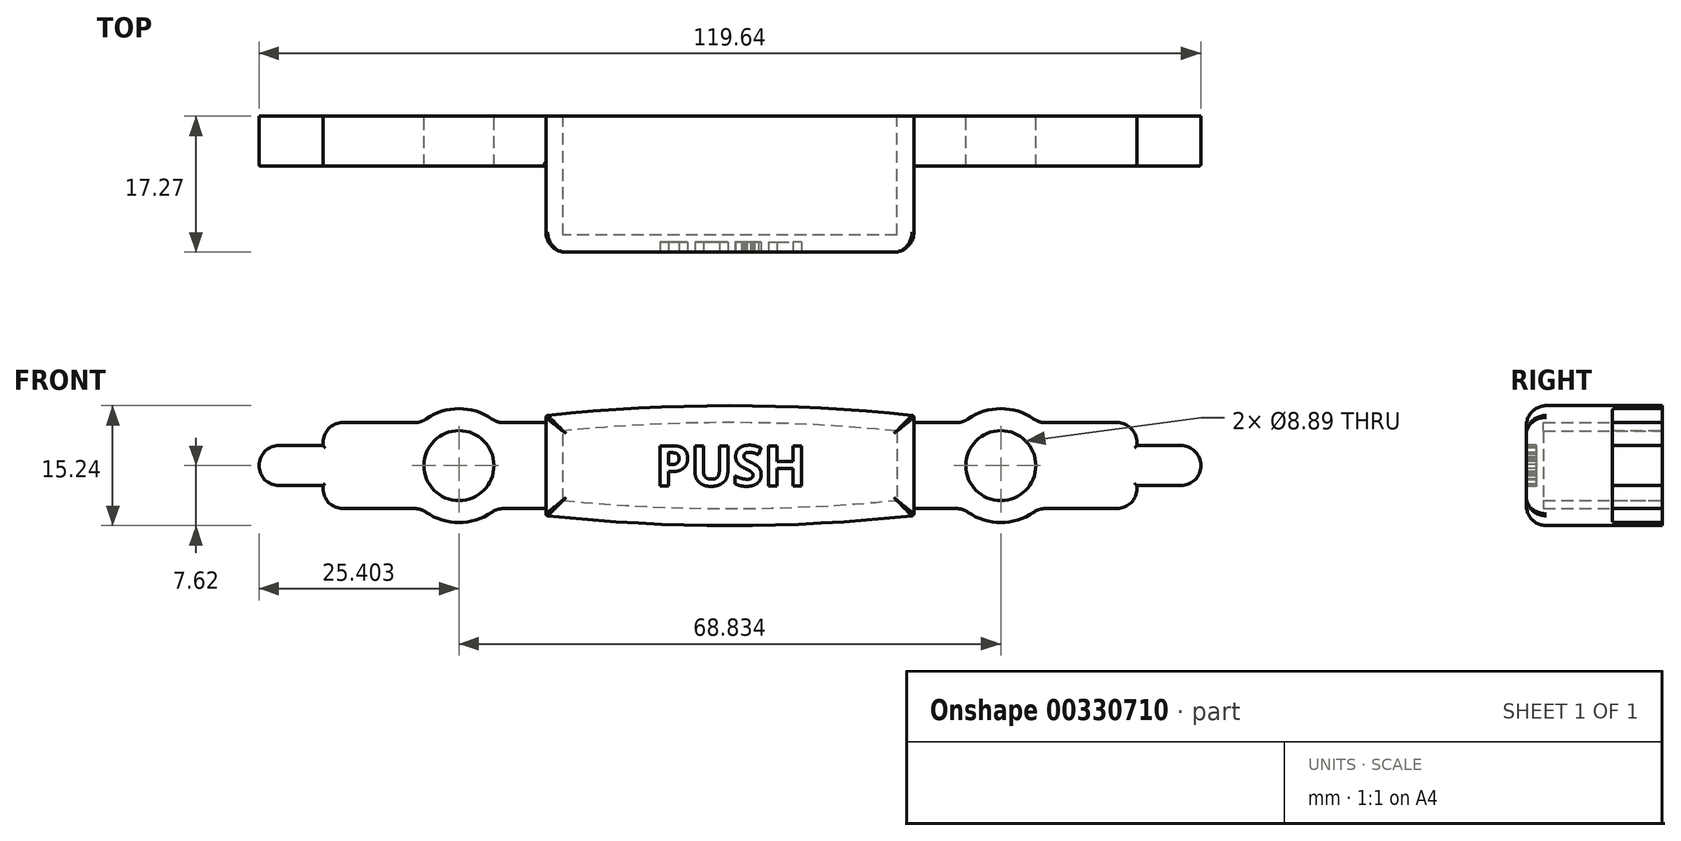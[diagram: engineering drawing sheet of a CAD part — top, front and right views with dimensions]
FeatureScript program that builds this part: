
annotation { "Feature Type Name" : "Feature", "Feature Type Description" : "" }
export const myFeature = defineFeature(function(context is Context, id is Id, definition is map)
    precondition{}
    {
        {
            var Q0;
            Q0=qCreatedBy(makeId("Front.planeOp"),FACE);
            var sketch = newSketch(context, id + "F0", { "sketchPlane" : qUnion([Q0])});
            skLineSegment(sketch, "E0", {"start": v(23.37, 6.35) * mm, "end": v(23.37, -6.35) * mm});
            skLineSegment(sketch, "E1", {"start": v(-23.37, -6.35) * mm, "end": v(-23.37, 6.35) * mm});
            skArc(sketch, "E2", {"start": v(23.37, 6.35) * mm, "mid": v(0, 7.62) * mm, "end": v(-23.37, 6.35) * mm});
            skArc(sketch, "E3", {"start": v(-23.37, -6.35) * mm, "mid": v(0, -7.62) * mm, "end": v(23.37, -6.35) * mm});
            skSolve(sketch);
        }
        {
            var Q0;
            Q0=qCreatedBy(makeId("Front.planeOp"),FACE);
            var sketch = newSketch(context, id + "F1", { "sketchPlane" : qUnion([Q0])});
            skLineSegment(sketch, "E4", {"start": v(23.26, 5.46) * mm, "end": v(29.67, 5.46) * mm});
            skLineSegment(sketch, "E5", {"start": v(51.69, 5.46) * mm, "end": v(51.69, 2.54) * mm});
            skLineSegment(sketch, "E6", {"start": v(51.69, -5.46) * mm, "end": v(39.17, -5.46) * mm});
            skLineSegment(sketch, "E7", {"start": v(51.69, -2.54) * mm, "end": v(59.82, -2.54) * mm});
            skLineSegment(sketch, "E8", {"start": v(59.82, 2.54) * mm, "end": v(59.82, -2.54) * mm});
            skLineSegment(sketch, "E9", {"start": v(59.82, 2.54) * mm, "end": v(51.69, 2.54) * mm});
            skCircle(sketch, "E10", {"center": v(34.42, 0) * mm, "radius": 4.44 * mm});
            skArc(sketch, "E11", {"start": v(29.67, -5.46) * mm, "mid": v(34.42, -7.24) * mm, "end": v(39.17, -5.46) * mm});
            skLineSegment(sketch, "E12.trimOffspring", {"start": v(51.69, -2.54) * mm, "end": v(51.69, -5.46) * mm});
            skLineSegment(sketch, "E13.trimOffspring", {"start": v(39.17, 5.46) * mm, "end": v(51.69, 5.46) * mm});
            skLineSegment(sketch, "E14.trimOffspring", {"start": v(29.67, -5.46) * mm, "end": v(23.26, -5.46) * mm});
            skLineSegment(sketch, "E15", {"start": v(23.26, 5.46) * mm, "end": v(23.26, -5.46) * mm});
            skArc(sketch, "E16.trimOffspring", {"start": v(39.17, 5.46) * mm, "mid": v(34.42, 7.24) * mm, "end": v(29.67, 5.46) * mm});
            skPoint(sketch, "E17.orphan", {"position": v(21.72, 5.46) * mm});
            skPoint(sketch, "E18.orphan", {"position": v(21.72, -5.46) * mm});
            skLineSegment(sketch, "E19.MirrorCS", {"start": v(-51.69, -2.54) * mm, "end": v(-51.69, -5.46) * mm});
            skLineSegment(sketch, "E20.MirrorCS", {"start": v(-51.69, 5.46) * mm, "end": v(-51.69, 2.54) * mm});
            skPoint(sketch, "E21.MirrorP", {"position": v(-21.72, 5.46) * mm});
            skLineSegment(sketch, "E22.MirrorCS", {"start": v(-23.26, 5.46) * mm, "end": v(-29.67, 5.46) * mm});
            skPoint(sketch, "E23.MirrorP", {"position": v(-21.72, -5.46) * mm});
            skArc(sketch, "E24.MirrorCS", {"start": v(-39.17, 5.46) * mm, "mid": v(-34.42, 7.24) * mm, "end": v(-29.67, 5.46) * mm});
            skLineSegment(sketch, "E25.MirrorCS", {"start": v(-59.82, 2.54) * mm, "end": v(-51.69, 2.54) * mm});
            skArc(sketch, "E26.MirrorCS", {"start": v(-29.67, -5.46) * mm, "mid": v(-34.42, -7.24) * mm, "end": v(-39.17, -5.46) * mm});
            skLineSegment(sketch, "E27.MirrorCS", {"start": v(-51.69, -5.46) * mm, "end": v(-39.17, -5.46) * mm});
            skCircle(sketch, "E28.MirrorC", {"center": v(-34.42, 0) * mm, "radius": 4.44 * mm});
            skLineSegment(sketch, "E29.MirrorCS", {"start": v(-39.17, 5.46) * mm, "end": v(-51.69, 5.46) * mm});
            skLineSegment(sketch, "E30.MirrorCS", {"start": v(-59.82, 2.54) * mm, "end": v(-59.82, -2.54) * mm});
            skLineSegment(sketch, "E31.MirrorCS", {"start": v(-51.69, -2.54) * mm, "end": v(-59.82, -2.54) * mm});
            skLineSegment(sketch, "E32.MirrorCS", {"start": v(-29.67, -5.46) * mm, "end": v(-23.26, -5.46) * mm});
            skLineSegment(sketch, "E33.MirrorCS", {"start": v(-23.26, 5.46) * mm, "end": v(-23.26, -5.46) * mm});
            skSolve(sketch);
        }
        {
            var Q0;
            Q0=makeQuery(id+"F0.imprint","IMPRINT",FACE,{"disambiguationData":[TD([[makeQuery(id+"F0.imprint","IMPRINT",EDGE,{"derivedFrom":sQuery(id+"F0.wireOp",EDGE,"E0")}),-1.0]])]});
            extrude(context, id + "F2", {"entities" : qUnion([Q0]), "depth" : 17.27 * mm});
        }
        {
            var Q0;
            Q0=makeQuery(id+"F2.opExtrude","CAP_FACE",FACE,{"disambiguationData":[OSD([sQuery(id+"F0.wireOp",EDGE,"E0"),sQuery(id+"F0.wireOp",EDGE,"E1"),sQuery(id+"F0.wireOp",EDGE,"E2"),sQuery(id+"F0.wireOp",EDGE,"E3")])],"isStart":true});
            shell(context, id + "F3", {"entities" : qUnion([Q0]), "thickness" : 2.16 * mm});
        }
        {
            var Q0;
            Q0 = qSketchRegion(id + "F1", true);
            extrude(context, id + "F4", {"entities" : qUnion([Q0]), "operationType" : NewBodyOperationType.ADD, "depth" : 6.35 * mm});
        }
        {
            var Q0;
            Q0=makeQuery(id+"F4.opExtrude","SWEPT_EDGE",EDGE,{"disambiguationData":[OSD([sQuery(id+"F1.wireOp",EDGE,"E30.MirrorCS"),sQuery(id+"F1.wireOp",EDGE,"E31.MirrorCS")])]});
            var Q1;
            Q1=makeQuery(id+"F4.opExtrude","SWEPT_EDGE",EDGE,{"disambiguationData":[OSD([sQuery(id+"F1.wireOp",EDGE,"E25.MirrorCS"),sQuery(id+"F1.wireOp",EDGE,"E30.MirrorCS")])]});
            var Q2;
            Q2=makeQuery(id+"F4.opExtrude","SWEPT_EDGE",EDGE,{"disambiguationData":[OSD([sQuery(id+"F1.wireOp",EDGE,"E7"),sQuery(id+"F1.wireOp",EDGE,"E8")])]});
            var Q3;
            Q3=makeQuery(id+"F4.opExtrude","SWEPT_EDGE",EDGE,{"disambiguationData":[OSD([sQuery(id+"F1.wireOp",EDGE,"E8"),sQuery(id+"F1.wireOp",EDGE,"E9")])]});
            var Q4;
            Q4=makeQuery(id+"F4.opExtrude","SWEPT_EDGE",EDGE,{"disambiguationData":[OSD([sQuery(id+"F1.wireOp",EDGE,"E5"),sQuery(id+"F1.wireOp",EDGE,"E13.trimOffspring")])]});
            var Q5;
            Q5=makeQuery(id+"F4.opExtrude","SWEPT_EDGE",EDGE,{"disambiguationData":[OSD([sQuery(id+"F1.wireOp",EDGE,"E6"),sQuery(id+"F1.wireOp",EDGE,"E12.trimOffspring")])]});
            var Q6;
            Q6=makeQuery(id+"F4.opExtrude","SWEPT_EDGE",EDGE,{"disambiguationData":[OSD([sQuery(id+"F1.wireOp",EDGE,"E20.MirrorCS"),sQuery(id+"F1.wireOp",EDGE,"E29.MirrorCS")])]});
            var Q7;
            Q7=makeQuery(id+"F4.opExtrude","SWEPT_EDGE",EDGE,{"disambiguationData":[OSD([sQuery(id+"F1.wireOp",EDGE,"E19.MirrorCS"),sQuery(id+"F1.wireOp",EDGE,"E27.MirrorCS")])]});
            var Q8;
            Q8=makeQuery(id+"F4.opExtrude","SWEPT_EDGE",EDGE,{"disambiguationData":[OSD([sQuery(id+"F1.wireOp",EDGE,"E26.MirrorCS"),sQuery(id+"F1.wireOp",EDGE,"E27.MirrorCS")])]});
            var Q9;
            Q9=makeQuery(id+"F4.opExtrude","SWEPT_EDGE",EDGE,{"disambiguationData":[OSD([sQuery(id+"F1.wireOp",EDGE,"E11"),sQuery(id+"F1.wireOp",EDGE,"E14.trimOffspring")])]});
            var Q10;
            Q10=makeQuery(id+"F4.opExtrude","SWEPT_EDGE",EDGE,{"disambiguationData":[OSD([sQuery(id+"F1.wireOp",EDGE,"E6"),sQuery(id+"F1.wireOp",EDGE,"E11")])]});
            var Q11;
            Q11=makeQuery(id+"F4.opExtrude","SWEPT_EDGE",EDGE,{"disambiguationData":[OSD([sQuery(id+"F1.wireOp",EDGE,"E26.MirrorCS"),sQuery(id+"F1.wireOp",EDGE,"E32.MirrorCS")])]});
            var Q12;
            Q12=makeQuery(id+"F4.opExtrude","SWEPT_EDGE",EDGE,{"disambiguationData":[OSD([sQuery(id+"F1.wireOp",EDGE,"E4"),sQuery(id+"F1.wireOp",EDGE,"E16.trimOffspring")])]});
            var Q13;
            Q13=makeQuery(id+"F4.opExtrude","SWEPT_EDGE",EDGE,{"disambiguationData":[OSD([sQuery(id+"F1.wireOp",EDGE,"E13.trimOffspring"),sQuery(id+"F1.wireOp",EDGE,"E16.trimOffspring")])]});
            var Q14;
            Q14=makeQuery(id+"F4.opExtrude","SWEPT_EDGE",EDGE,{"disambiguationData":[OSD([sQuery(id+"F1.wireOp",EDGE,"E22.MirrorCS"),sQuery(id+"F1.wireOp",EDGE,"E24.MirrorCS")])]});
            var Q15;
            Q15=makeQuery(id+"F4.opExtrude","SWEPT_EDGE",EDGE,{"disambiguationData":[OSD([sQuery(id+"F1.wireOp",EDGE,"E24.MirrorCS"),sQuery(id+"F1.wireOp",EDGE,"E29.MirrorCS")])]});
            fillet(context, id + "F5", {"entities" : qUnion([Q0, Q1, Q2, Q3, Q4, Q5, Q6, Q7, Q8, Q9, Q10, Q11, Q12, Q13, Q14, Q15]), "radius" : 2.54 * mm, "tangentPropagation" : true, "allowEdgeOverflow" : false});
        }
        {
            var Q0;
            Q0=makeQuery(id+"F2.opExtrude","SWEPT_EDGE",EDGE,{"disambiguationData":[OSD([sQuery(id+"F0.wireOp",EDGE,"E1"),sQuery(id+"F0.wireOp",EDGE,"E2")])]});
            var Q1;
            Q1=makeQuery(id+"F2.opExtrude","SWEPT_EDGE",EDGE,{"disambiguationData":[OSD([sQuery(id+"F0.wireOp",EDGE,"E0"),sQuery(id+"F0.wireOp",EDGE,"E2")])]});
            var Q2;
            Q2=makeQuery(id+"F2.opExtrude","SWEPT_EDGE",EDGE,{"disambiguationData":[OSD([sQuery(id+"F0.wireOp",EDGE,"E1"),sQuery(id+"F0.wireOp",EDGE,"E3")])]});
            var Q3;
            Q3=makeQuery(id+"F2.opExtrude","SWEPT_EDGE",EDGE,{"disambiguationData":[OSD([sQuery(id+"F0.wireOp",EDGE,"E0"),sQuery(id+"F0.wireOp",EDGE,"E3")])]});
            var Q4;
            Q4=makeQuery(id+"F4.opExtrude","CAP_EDGE",EDGE,{"disambiguationData":[OSD([sQuery(id+"F1.wireOp",EDGE,"E27.MirrorCS")])],"isStart":false});
            var Q5;
            Q5=makeQuery(id+"F4.opExtrude","CAP_EDGE",EDGE,{"disambiguationData":[OSD([sQuery(id+"F1.wireOp",EDGE,"E29.MirrorCS")])],"isStart":false});
            var Q6;
            Q6=makeQuery(id+"F4.opExtrude","CAP_EDGE",EDGE,{"disambiguationData":[OSD([sQuery(id+"F1.wireOp",EDGE,"E25.MirrorCS")])],"isStart":false});
            var Q7;
            {var subQ0=sQuery(id+"F1.wireOp",EDGE,"E29.MirrorCS");var subQ1=sQuery(id+"F1.wireOp",EDGE,"E24.MirrorCS");Q7=makeQuery(id+"F5.opFillet","BLEND_EDGE",EDGE,{"blendedFrom":[makeQuery(id+"F4.opExtrude","SWEPT_EDGE",EDGE,{"disambiguationData":[OSD([subQ1,subQ0])]}),makeQuery(id+"F4.opExtrude","CAP_FACE",FACE,{"disambiguationData":[OSD([sQuery(id+"F1.wireOp",EDGE,"E19.MirrorCS"),sQuery(id+"F1.wireOp",EDGE,"E20.MirrorCS"),sQuery(id+"F1.wireOp",EDGE,"E22.MirrorCS"),subQ1,sQuery(id+"F1.wireOp",EDGE,"E25.MirrorCS"),sQuery(id+"F1.wireOp",EDGE,"E26.MirrorCS"),sQuery(id+"F1.wireOp",EDGE,"E27.MirrorCS"),sQuery(id+"F1.wireOp",EDGE,"E28.MirrorC"),subQ0,sQuery(id+"F1.wireOp",EDGE,"E30.MirrorCS"),sQuery(id+"F1.wireOp",EDGE,"E31.MirrorCS"),sQuery(id+"F1.wireOp",EDGE,"E32.MirrorCS"),sQuery(id+"F1.wireOp",EDGE,"E33.MirrorCS")])],"isStart":false})],"blendedInto":[makeQuery(id+"F4.opExtrude","CAP_FACE",FACE,{"disambiguationData":[OSD([sQuery(id+"F1.wireOp",EDGE,"E19.MirrorCS"),sQuery(id+"F1.wireOp",EDGE,"E20.MirrorCS"),sQuery(id+"F1.wireOp",EDGE,"E22.MirrorCS"),subQ1,sQuery(id+"F1.wireOp",EDGE,"E25.MirrorCS"),sQuery(id+"F1.wireOp",EDGE,"E26.MirrorCS"),sQuery(id+"F1.wireOp",EDGE,"E27.MirrorCS"),sQuery(id+"F1.wireOp",EDGE,"E28.MirrorC"),subQ0,sQuery(id+"F1.wireOp",EDGE,"E30.MirrorCS"),sQuery(id+"F1.wireOp",EDGE,"E31.MirrorCS"),sQuery(id+"F1.wireOp",EDGE,"E32.MirrorCS"),sQuery(id+"F1.wireOp",EDGE,"E33.MirrorCS")])],"isStart":false})]});}
            var Q8;
            {var subQ0=sQuery(id+"F1.wireOp",EDGE,"E31.MirrorCS");var subQ1=sQuery(id+"F1.wireOp",EDGE,"E30.MirrorCS");Q8=makeQuery(id+"F5.opFillet","BLEND_EDGE",EDGE,{"blendedFrom":[makeQuery(id+"F4.opExtrude","SWEPT_EDGE",EDGE,{"disambiguationData":[OSD([subQ1,subQ0])]}),makeQuery(id+"F4.opExtrude","CAP_FACE",FACE,{"disambiguationData":[OSD([sQuery(id+"F1.wireOp",EDGE,"E19.MirrorCS"),sQuery(id+"F1.wireOp",EDGE,"E20.MirrorCS"),sQuery(id+"F1.wireOp",EDGE,"E22.MirrorCS"),sQuery(id+"F1.wireOp",EDGE,"E24.MirrorCS"),sQuery(id+"F1.wireOp",EDGE,"E25.MirrorCS"),sQuery(id+"F1.wireOp",EDGE,"E26.MirrorCS"),sQuery(id+"F1.wireOp",EDGE,"E27.MirrorCS"),sQuery(id+"F1.wireOp",EDGE,"E28.MirrorC"),sQuery(id+"F1.wireOp",EDGE,"E29.MirrorCS"),subQ1,subQ0,sQuery(id+"F1.wireOp",EDGE,"E32.MirrorCS"),sQuery(id+"F1.wireOp",EDGE,"E33.MirrorCS")])],"isStart":false})],"blendedInto":[makeQuery(id+"F4.opExtrude","CAP_FACE",FACE,{"disambiguationData":[OSD([sQuery(id+"F1.wireOp",EDGE,"E19.MirrorCS"),sQuery(id+"F1.wireOp",EDGE,"E20.MirrorCS"),sQuery(id+"F1.wireOp",EDGE,"E22.MirrorCS"),sQuery(id+"F1.wireOp",EDGE,"E24.MirrorCS"),sQuery(id+"F1.wireOp",EDGE,"E25.MirrorCS"),sQuery(id+"F1.wireOp",EDGE,"E26.MirrorCS"),sQuery(id+"F1.wireOp",EDGE,"E27.MirrorCS"),sQuery(id+"F1.wireOp",EDGE,"E28.MirrorC"),sQuery(id+"F1.wireOp",EDGE,"E29.MirrorCS"),subQ1,subQ0,sQuery(id+"F1.wireOp",EDGE,"E32.MirrorCS"),sQuery(id+"F1.wireOp",EDGE,"E33.MirrorCS")])],"isStart":false})]});}
            var Q9;
            {var subQ0=sQuery(id+"F1.wireOp",EDGE,"E29.MirrorCS");var subQ1=sQuery(id+"F1.wireOp",EDGE,"E20.MirrorCS");Q9=makeQuery(id+"F5.opFillet","BLEND_EDGE",EDGE,{"blendedFrom":[makeQuery(id+"F4.opExtrude","SWEPT_EDGE",EDGE,{"disambiguationData":[OSD([subQ1,subQ0])]}),makeQuery(id+"F4.opExtrude","CAP_FACE",FACE,{"disambiguationData":[OSD([sQuery(id+"F1.wireOp",EDGE,"E19.MirrorCS"),subQ1,sQuery(id+"F1.wireOp",EDGE,"E22.MirrorCS"),sQuery(id+"F1.wireOp",EDGE,"E24.MirrorCS"),sQuery(id+"F1.wireOp",EDGE,"E25.MirrorCS"),sQuery(id+"F1.wireOp",EDGE,"E26.MirrorCS"),sQuery(id+"F1.wireOp",EDGE,"E27.MirrorCS"),sQuery(id+"F1.wireOp",EDGE,"E28.MirrorC"),subQ0,sQuery(id+"F1.wireOp",EDGE,"E30.MirrorCS"),sQuery(id+"F1.wireOp",EDGE,"E31.MirrorCS"),sQuery(id+"F1.wireOp",EDGE,"E32.MirrorCS"),sQuery(id+"F1.wireOp",EDGE,"E33.MirrorCS")])],"isStart":false})],"blendedInto":[makeQuery(id+"F4.opExtrude","CAP_FACE",FACE,{"disambiguationData":[OSD([sQuery(id+"F1.wireOp",EDGE,"E19.MirrorCS"),subQ1,sQuery(id+"F1.wireOp",EDGE,"E22.MirrorCS"),sQuery(id+"F1.wireOp",EDGE,"E24.MirrorCS"),sQuery(id+"F1.wireOp",EDGE,"E25.MirrorCS"),sQuery(id+"F1.wireOp",EDGE,"E26.MirrorCS"),sQuery(id+"F1.wireOp",EDGE,"E27.MirrorCS"),sQuery(id+"F1.wireOp",EDGE,"E28.MirrorC"),subQ0,sQuery(id+"F1.wireOp",EDGE,"E30.MirrorCS"),sQuery(id+"F1.wireOp",EDGE,"E31.MirrorCS"),sQuery(id+"F1.wireOp",EDGE,"E32.MirrorCS"),sQuery(id+"F1.wireOp",EDGE,"E33.MirrorCS")])],"isStart":false})]});}
            var Q10;
            {var subQ0=sQuery(id+"F1.wireOp",EDGE,"E27.MirrorCS");var subQ1=sQuery(id+"F1.wireOp",EDGE,"E19.MirrorCS");Q10=makeQuery(id+"F5.opFillet","BLEND_EDGE",EDGE,{"blendedFrom":[makeQuery(id+"F4.opExtrude","SWEPT_EDGE",EDGE,{"disambiguationData":[OSD([subQ1,subQ0])]}),makeQuery(id+"F4.opExtrude","CAP_FACE",FACE,{"disambiguationData":[OSD([subQ1,sQuery(id+"F1.wireOp",EDGE,"E20.MirrorCS"),sQuery(id+"F1.wireOp",EDGE,"E22.MirrorCS"),sQuery(id+"F1.wireOp",EDGE,"E24.MirrorCS"),sQuery(id+"F1.wireOp",EDGE,"E25.MirrorCS"),sQuery(id+"F1.wireOp",EDGE,"E26.MirrorCS"),subQ0,sQuery(id+"F1.wireOp",EDGE,"E28.MirrorC"),sQuery(id+"F1.wireOp",EDGE,"E29.MirrorCS"),sQuery(id+"F1.wireOp",EDGE,"E30.MirrorCS"),sQuery(id+"F1.wireOp",EDGE,"E31.MirrorCS"),sQuery(id+"F1.wireOp",EDGE,"E32.MirrorCS"),sQuery(id+"F1.wireOp",EDGE,"E33.MirrorCS")])],"isStart":false})],"blendedInto":[makeQuery(id+"F4.opExtrude","CAP_FACE",FACE,{"disambiguationData":[OSD([subQ1,sQuery(id+"F1.wireOp",EDGE,"E20.MirrorCS"),sQuery(id+"F1.wireOp",EDGE,"E22.MirrorCS"),sQuery(id+"F1.wireOp",EDGE,"E24.MirrorCS"),sQuery(id+"F1.wireOp",EDGE,"E25.MirrorCS"),sQuery(id+"F1.wireOp",EDGE,"E26.MirrorCS"),subQ0,sQuery(id+"F1.wireOp",EDGE,"E28.MirrorC"),sQuery(id+"F1.wireOp",EDGE,"E29.MirrorCS"),sQuery(id+"F1.wireOp",EDGE,"E30.MirrorCS"),sQuery(id+"F1.wireOp",EDGE,"E31.MirrorCS"),sQuery(id+"F1.wireOp",EDGE,"E32.MirrorCS"),sQuery(id+"F1.wireOp",EDGE,"E33.MirrorCS")])],"isStart":false})]});}
            var Q11;
            Q11=makeQuery(id+"F4.opExtrude","CAP_EDGE",EDGE,{"disambiguationData":[OSD([sQuery(id+"F1.wireOp",EDGE,"E19.MirrorCS")])],"isStart":false});
            var Q12;
            Q12=makeQuery(id+"F4.opExtrude","CAP_EDGE",EDGE,{"disambiguationData":[OSD([sQuery(id+"F1.wireOp",EDGE,"E20.MirrorCS")])],"isStart":false});
            var Q13;
            Q13=makeQuery(id+"F4.opExtrude","CAP_EDGE",EDGE,{"disambiguationData":[OSD([sQuery(id+"F1.wireOp",EDGE,"E31.MirrorCS")])],"isStart":false});
            var Q14;
            {var subQ0=sQuery(id+"F1.wireOp",EDGE,"E27.MirrorCS");var subQ1=sQuery(id+"F1.wireOp",EDGE,"E26.MirrorCS");Q14=makeQuery(id+"F5.opFillet","BLEND_EDGE",EDGE,{"blendedFrom":[makeQuery(id+"F4.opExtrude","SWEPT_EDGE",EDGE,{"disambiguationData":[OSD([subQ1,subQ0])]}),makeQuery(id+"F4.opExtrude","CAP_FACE",FACE,{"disambiguationData":[OSD([sQuery(id+"F1.wireOp",EDGE,"E19.MirrorCS"),sQuery(id+"F1.wireOp",EDGE,"E20.MirrorCS"),sQuery(id+"F1.wireOp",EDGE,"E22.MirrorCS"),sQuery(id+"F1.wireOp",EDGE,"E24.MirrorCS"),sQuery(id+"F1.wireOp",EDGE,"E25.MirrorCS"),subQ1,subQ0,sQuery(id+"F1.wireOp",EDGE,"E28.MirrorC"),sQuery(id+"F1.wireOp",EDGE,"E29.MirrorCS"),sQuery(id+"F1.wireOp",EDGE,"E30.MirrorCS"),sQuery(id+"F1.wireOp",EDGE,"E31.MirrorCS"),sQuery(id+"F1.wireOp",EDGE,"E32.MirrorCS"),sQuery(id+"F1.wireOp",EDGE,"E33.MirrorCS")])],"isStart":false})],"blendedInto":[makeQuery(id+"F4.opExtrude","CAP_FACE",FACE,{"disambiguationData":[OSD([sQuery(id+"F1.wireOp",EDGE,"E19.MirrorCS"),sQuery(id+"F1.wireOp",EDGE,"E20.MirrorCS"),sQuery(id+"F1.wireOp",EDGE,"E22.MirrorCS"),sQuery(id+"F1.wireOp",EDGE,"E24.MirrorCS"),sQuery(id+"F1.wireOp",EDGE,"E25.MirrorCS"),subQ1,subQ0,sQuery(id+"F1.wireOp",EDGE,"E28.MirrorC"),sQuery(id+"F1.wireOp",EDGE,"E29.MirrorCS"),sQuery(id+"F1.wireOp",EDGE,"E30.MirrorCS"),sQuery(id+"F1.wireOp",EDGE,"E31.MirrorCS"),sQuery(id+"F1.wireOp",EDGE,"E32.MirrorCS"),sQuery(id+"F1.wireOp",EDGE,"E33.MirrorCS")])],"isStart":false})]});}
            var Q15;
            Q15=makeQuery(id+"F4.opExtrude","CAP_EDGE",EDGE,{"disambiguationData":[OSD([sQuery(id+"F1.wireOp",EDGE,"E26.MirrorCS")])],"isStart":false});
            var Q16;
            {var subQ0=sQuery(id+"F1.wireOp",EDGE,"E32.MirrorCS");var subQ1=sQuery(id+"F1.wireOp",EDGE,"E26.MirrorCS");Q16=makeQuery(id+"F5.opFillet","BLEND_EDGE",EDGE,{"blendedFrom":[makeQuery(id+"F4.opExtrude","SWEPT_EDGE",EDGE,{"disambiguationData":[OSD([subQ1,subQ0])]}),makeQuery(id+"F4.opExtrude","CAP_FACE",FACE,{"disambiguationData":[OSD([sQuery(id+"F1.wireOp",EDGE,"E19.MirrorCS"),sQuery(id+"F1.wireOp",EDGE,"E20.MirrorCS"),sQuery(id+"F1.wireOp",EDGE,"E22.MirrorCS"),sQuery(id+"F1.wireOp",EDGE,"E24.MirrorCS"),sQuery(id+"F1.wireOp",EDGE,"E25.MirrorCS"),subQ1,sQuery(id+"F1.wireOp",EDGE,"E27.MirrorCS"),sQuery(id+"F1.wireOp",EDGE,"E28.MirrorC"),sQuery(id+"F1.wireOp",EDGE,"E29.MirrorCS"),sQuery(id+"F1.wireOp",EDGE,"E30.MirrorCS"),sQuery(id+"F1.wireOp",EDGE,"E31.MirrorCS"),subQ0,sQuery(id+"F1.wireOp",EDGE,"E33.MirrorCS")])],"isStart":false})],"blendedInto":[makeQuery(id+"F4.opExtrude","CAP_FACE",FACE,{"disambiguationData":[OSD([sQuery(id+"F1.wireOp",EDGE,"E19.MirrorCS"),sQuery(id+"F1.wireOp",EDGE,"E20.MirrorCS"),sQuery(id+"F1.wireOp",EDGE,"E22.MirrorCS"),sQuery(id+"F1.wireOp",EDGE,"E24.MirrorCS"),sQuery(id+"F1.wireOp",EDGE,"E25.MirrorCS"),subQ1,sQuery(id+"F1.wireOp",EDGE,"E27.MirrorCS"),sQuery(id+"F1.wireOp",EDGE,"E28.MirrorC"),sQuery(id+"F1.wireOp",EDGE,"E29.MirrorCS"),sQuery(id+"F1.wireOp",EDGE,"E30.MirrorCS"),sQuery(id+"F1.wireOp",EDGE,"E31.MirrorCS"),subQ0,sQuery(id+"F1.wireOp",EDGE,"E33.MirrorCS")])],"isStart":false})]});}
            var Q17;
            Q17=makeQuery(id+"F4.opExtrude","CAP_EDGE",EDGE,{"disambiguationData":[OSD([sQuery(id+"F1.wireOp",EDGE,"E32.MirrorCS")])],"isStart":false});
            var Q18;
            Q18=makeQuery(id+"F4.opExtrude","CAP_EDGE",EDGE,{"disambiguationData":[OSD([sQuery(id+"F1.wireOp",EDGE,"E24.MirrorCS")])],"isStart":false});
            var Q19;
            {var subQ0=sQuery(id+"F1.wireOp",EDGE,"E24.MirrorCS");var subQ1=sQuery(id+"F1.wireOp",EDGE,"E22.MirrorCS");Q19=makeQuery(id+"F5.opFillet","BLEND_EDGE",EDGE,{"blendedFrom":[makeQuery(id+"F4.opExtrude","SWEPT_EDGE",EDGE,{"disambiguationData":[OSD([subQ1,subQ0])]}),makeQuery(id+"F4.opExtrude","CAP_FACE",FACE,{"disambiguationData":[OSD([sQuery(id+"F1.wireOp",EDGE,"E19.MirrorCS"),sQuery(id+"F1.wireOp",EDGE,"E20.MirrorCS"),subQ1,subQ0,sQuery(id+"F1.wireOp",EDGE,"E25.MirrorCS"),sQuery(id+"F1.wireOp",EDGE,"E26.MirrorCS"),sQuery(id+"F1.wireOp",EDGE,"E27.MirrorCS"),sQuery(id+"F1.wireOp",EDGE,"E28.MirrorC"),sQuery(id+"F1.wireOp",EDGE,"E29.MirrorCS"),sQuery(id+"F1.wireOp",EDGE,"E30.MirrorCS"),sQuery(id+"F1.wireOp",EDGE,"E31.MirrorCS"),sQuery(id+"F1.wireOp",EDGE,"E32.MirrorCS"),sQuery(id+"F1.wireOp",EDGE,"E33.MirrorCS")])],"isStart":false})],"blendedInto":[makeQuery(id+"F4.opExtrude","CAP_FACE",FACE,{"disambiguationData":[OSD([sQuery(id+"F1.wireOp",EDGE,"E19.MirrorCS"),sQuery(id+"F1.wireOp",EDGE,"E20.MirrorCS"),subQ1,subQ0,sQuery(id+"F1.wireOp",EDGE,"E25.MirrorCS"),sQuery(id+"F1.wireOp",EDGE,"E26.MirrorCS"),sQuery(id+"F1.wireOp",EDGE,"E27.MirrorCS"),sQuery(id+"F1.wireOp",EDGE,"E28.MirrorC"),sQuery(id+"F1.wireOp",EDGE,"E29.MirrorCS"),sQuery(id+"F1.wireOp",EDGE,"E30.MirrorCS"),sQuery(id+"F1.wireOp",EDGE,"E31.MirrorCS"),sQuery(id+"F1.wireOp",EDGE,"E32.MirrorCS"),sQuery(id+"F1.wireOp",EDGE,"E33.MirrorCS")])],"isStart":false})]});}
            var Q20;
            Q20=makeQuery(id+"F4.boolean.opBoolean","INTERSECT",EDGE,{"derivedFrom":[makeQuery(id+"F2.opExtrude","SWEPT_FACE",FACE,{"disambiguationData":[OSD([sQuery(id+"F0.wireOp",EDGE,"E1")])]}),makeQuery(id+"F4.opExtrude","CAP_FACE",FACE,{"disambiguationData":[OSD([sQuery(id+"F1.wireOp",EDGE,"E19.MirrorCS"),sQuery(id+"F1.wireOp",EDGE,"E20.MirrorCS"),sQuery(id+"F1.wireOp",EDGE,"E22.MirrorCS"),sQuery(id+"F1.wireOp",EDGE,"E24.MirrorCS"),sQuery(id+"F1.wireOp",EDGE,"E25.MirrorCS"),sQuery(id+"F1.wireOp",EDGE,"E26.MirrorCS"),sQuery(id+"F1.wireOp",EDGE,"E27.MirrorCS"),sQuery(id+"F1.wireOp",EDGE,"E28.MirrorC"),sQuery(id+"F1.wireOp",EDGE,"E29.MirrorCS"),sQuery(id+"F1.wireOp",EDGE,"E30.MirrorCS"),sQuery(id+"F1.wireOp",EDGE,"E31.MirrorCS"),sQuery(id+"F1.wireOp",EDGE,"E32.MirrorCS"),sQuery(id+"F1.wireOp",EDGE,"E33.MirrorCS")])],"isStart":false})]});
            var Q21;
            Q21=makeQuery(id+"F4.opExtrude","CAP_EDGE",EDGE,{"disambiguationData":[OSD([sQuery(id+"F1.wireOp",EDGE,"E4")])],"isStart":false});
            var Q22;
            Q22=makeQuery(id+"F4.opExtrude","CAP_EDGE",EDGE,{"disambiguationData":[OSD([sQuery(id+"F1.wireOp",EDGE,"E14.trimOffspring")])],"isStart":false});
            var Q23;
            {var subQ0=sQuery(id+"F1.wireOp",EDGE,"E16.trimOffspring");var subQ1=sQuery(id+"F1.wireOp",EDGE,"E4");Q23=makeQuery(id+"F5.opFillet","BLEND_EDGE",EDGE,{"blendedFrom":[makeQuery(id+"F4.opExtrude","SWEPT_EDGE",EDGE,{"disambiguationData":[OSD([subQ1,subQ0])]}),makeQuery(id+"F4.opExtrude","CAP_FACE",FACE,{"disambiguationData":[OSD([subQ1,sQuery(id+"F1.wireOp",EDGE,"E5"),sQuery(id+"F1.wireOp",EDGE,"E6"),sQuery(id+"F1.wireOp",EDGE,"E7"),sQuery(id+"F1.wireOp",EDGE,"E8"),sQuery(id+"F1.wireOp",EDGE,"E9"),sQuery(id+"F1.wireOp",EDGE,"E10"),sQuery(id+"F1.wireOp",EDGE,"E11"),sQuery(id+"F1.wireOp",EDGE,"E12.trimOffspring"),sQuery(id+"F1.wireOp",EDGE,"E13.trimOffspring"),sQuery(id+"F1.wireOp",EDGE,"E14.trimOffspring"),sQuery(id+"F1.wireOp",EDGE,"E15"),subQ0])],"isStart":false})],"blendedInto":[makeQuery(id+"F4.opExtrude","CAP_FACE",FACE,{"disambiguationData":[OSD([subQ1,sQuery(id+"F1.wireOp",EDGE,"E5"),sQuery(id+"F1.wireOp",EDGE,"E6"),sQuery(id+"F1.wireOp",EDGE,"E7"),sQuery(id+"F1.wireOp",EDGE,"E8"),sQuery(id+"F1.wireOp",EDGE,"E9"),sQuery(id+"F1.wireOp",EDGE,"E10"),sQuery(id+"F1.wireOp",EDGE,"E11"),sQuery(id+"F1.wireOp",EDGE,"E12.trimOffspring"),sQuery(id+"F1.wireOp",EDGE,"E13.trimOffspring"),sQuery(id+"F1.wireOp",EDGE,"E14.trimOffspring"),sQuery(id+"F1.wireOp",EDGE,"E15"),subQ0])],"isStart":false})]});}
            var Q24;
            Q24=makeQuery(id+"F4.opExtrude","CAP_EDGE",EDGE,{"disambiguationData":[OSD([sQuery(id+"F1.wireOp",EDGE,"E16.trimOffspring")])],"isStart":false});
            var Q25;
            {var subQ0=sQuery(id+"F1.wireOp",EDGE,"E16.trimOffspring");var subQ1=sQuery(id+"F1.wireOp",EDGE,"E13.trimOffspring");Q25=makeQuery(id+"F5.opFillet","BLEND_EDGE",EDGE,{"blendedFrom":[makeQuery(id+"F4.opExtrude","SWEPT_EDGE",EDGE,{"disambiguationData":[OSD([subQ1,subQ0])]}),makeQuery(id+"F4.opExtrude","CAP_FACE",FACE,{"disambiguationData":[OSD([sQuery(id+"F1.wireOp",EDGE,"E4"),sQuery(id+"F1.wireOp",EDGE,"E5"),sQuery(id+"F1.wireOp",EDGE,"E6"),sQuery(id+"F1.wireOp",EDGE,"E7"),sQuery(id+"F1.wireOp",EDGE,"E8"),sQuery(id+"F1.wireOp",EDGE,"E9"),sQuery(id+"F1.wireOp",EDGE,"E10"),sQuery(id+"F1.wireOp",EDGE,"E11"),sQuery(id+"F1.wireOp",EDGE,"E12.trimOffspring"),subQ1,sQuery(id+"F1.wireOp",EDGE,"E14.trimOffspring"),sQuery(id+"F1.wireOp",EDGE,"E15"),subQ0])],"isStart":false})],"blendedInto":[makeQuery(id+"F4.opExtrude","CAP_FACE",FACE,{"disambiguationData":[OSD([sQuery(id+"F1.wireOp",EDGE,"E4"),sQuery(id+"F1.wireOp",EDGE,"E5"),sQuery(id+"F1.wireOp",EDGE,"E6"),sQuery(id+"F1.wireOp",EDGE,"E7"),sQuery(id+"F1.wireOp",EDGE,"E8"),sQuery(id+"F1.wireOp",EDGE,"E9"),sQuery(id+"F1.wireOp",EDGE,"E10"),sQuery(id+"F1.wireOp",EDGE,"E11"),sQuery(id+"F1.wireOp",EDGE,"E12.trimOffspring"),subQ1,sQuery(id+"F1.wireOp",EDGE,"E14.trimOffspring"),sQuery(id+"F1.wireOp",EDGE,"E15"),subQ0])],"isStart":false})]});}
            var Q26;
            Q26=makeQuery(id+"F4.opExtrude","CAP_EDGE",EDGE,{"disambiguationData":[OSD([sQuery(id+"F1.wireOp",EDGE,"E13.trimOffspring")])],"isStart":false});
            var Q27;
            {var subQ0=sQuery(id+"F1.wireOp",EDGE,"E13.trimOffspring");var subQ1=sQuery(id+"F1.wireOp",EDGE,"E5");Q27=makeQuery(id+"F5.opFillet","BLEND_EDGE",EDGE,{"blendedFrom":[makeQuery(id+"F4.opExtrude","SWEPT_EDGE",EDGE,{"disambiguationData":[OSD([subQ1,subQ0])]}),makeQuery(id+"F4.opExtrude","CAP_FACE",FACE,{"disambiguationData":[OSD([sQuery(id+"F1.wireOp",EDGE,"E4"),subQ1,sQuery(id+"F1.wireOp",EDGE,"E6"),sQuery(id+"F1.wireOp",EDGE,"E7"),sQuery(id+"F1.wireOp",EDGE,"E8"),sQuery(id+"F1.wireOp",EDGE,"E9"),sQuery(id+"F1.wireOp",EDGE,"E10"),sQuery(id+"F1.wireOp",EDGE,"E11"),sQuery(id+"F1.wireOp",EDGE,"E12.trimOffspring"),subQ0,sQuery(id+"F1.wireOp",EDGE,"E14.trimOffspring"),sQuery(id+"F1.wireOp",EDGE,"E15"),sQuery(id+"F1.wireOp",EDGE,"E16.trimOffspring")])],"isStart":false})],"blendedInto":[makeQuery(id+"F4.opExtrude","CAP_FACE",FACE,{"disambiguationData":[OSD([sQuery(id+"F1.wireOp",EDGE,"E4"),subQ1,sQuery(id+"F1.wireOp",EDGE,"E6"),sQuery(id+"F1.wireOp",EDGE,"E7"),sQuery(id+"F1.wireOp",EDGE,"E8"),sQuery(id+"F1.wireOp",EDGE,"E9"),sQuery(id+"F1.wireOp",EDGE,"E10"),sQuery(id+"F1.wireOp",EDGE,"E11"),sQuery(id+"F1.wireOp",EDGE,"E12.trimOffspring"),subQ0,sQuery(id+"F1.wireOp",EDGE,"E14.trimOffspring"),sQuery(id+"F1.wireOp",EDGE,"E15"),sQuery(id+"F1.wireOp",EDGE,"E16.trimOffspring")])],"isStart":false})]});}
            var Q28;
            Q28=makeQuery(id+"F4.opExtrude","CAP_EDGE",EDGE,{"disambiguationData":[OSD([sQuery(id+"F1.wireOp",EDGE,"E5")])],"isStart":false});
            var Q29;
            Q29=makeQuery(id+"F4.opExtrude","CAP_EDGE",EDGE,{"disambiguationData":[OSD([sQuery(id+"F1.wireOp",EDGE,"E9")])],"isStart":false});
            var Q30;
            {var subQ0=sQuery(id+"F1.wireOp",EDGE,"E9");var subQ1=sQuery(id+"F1.wireOp",EDGE,"E8");Q30=makeQuery(id+"F5.opFillet","BLEND_EDGE",EDGE,{"blendedFrom":[makeQuery(id+"F4.opExtrude","SWEPT_EDGE",EDGE,{"disambiguationData":[OSD([subQ1,subQ0])]}),makeQuery(id+"F4.opExtrude","CAP_FACE",FACE,{"disambiguationData":[OSD([sQuery(id+"F1.wireOp",EDGE,"E4"),sQuery(id+"F1.wireOp",EDGE,"E5"),sQuery(id+"F1.wireOp",EDGE,"E6"),sQuery(id+"F1.wireOp",EDGE,"E7"),subQ1,subQ0,sQuery(id+"F1.wireOp",EDGE,"E10"),sQuery(id+"F1.wireOp",EDGE,"E11"),sQuery(id+"F1.wireOp",EDGE,"E12.trimOffspring"),sQuery(id+"F1.wireOp",EDGE,"E13.trimOffspring"),sQuery(id+"F1.wireOp",EDGE,"E14.trimOffspring"),sQuery(id+"F1.wireOp",EDGE,"E15"),sQuery(id+"F1.wireOp",EDGE,"E16.trimOffspring")])],"isStart":false})],"blendedInto":[makeQuery(id+"F4.opExtrude","CAP_FACE",FACE,{"disambiguationData":[OSD([sQuery(id+"F1.wireOp",EDGE,"E4"),sQuery(id+"F1.wireOp",EDGE,"E5"),sQuery(id+"F1.wireOp",EDGE,"E6"),sQuery(id+"F1.wireOp",EDGE,"E7"),subQ1,subQ0,sQuery(id+"F1.wireOp",EDGE,"E10"),sQuery(id+"F1.wireOp",EDGE,"E11"),sQuery(id+"F1.wireOp",EDGE,"E12.trimOffspring"),sQuery(id+"F1.wireOp",EDGE,"E13.trimOffspring"),sQuery(id+"F1.wireOp",EDGE,"E14.trimOffspring"),sQuery(id+"F1.wireOp",EDGE,"E15"),sQuery(id+"F1.wireOp",EDGE,"E16.trimOffspring")])],"isStart":false})]});}
            var Q31;
            Q31=makeQuery(id+"F4.opExtrude","CAP_EDGE",EDGE,{"disambiguationData":[OSD([sQuery(id+"F1.wireOp",EDGE,"E7")])],"isStart":false});
            var Q32;
            Q32=makeQuery(id+"F4.opExtrude","CAP_EDGE",EDGE,{"disambiguationData":[OSD([sQuery(id+"F1.wireOp",EDGE,"E12.trimOffspring")])],"isStart":false});
            var Q33;
            {var subQ0=sQuery(id+"F1.wireOp",EDGE,"E12.trimOffspring");var subQ1=sQuery(id+"F1.wireOp",EDGE,"E6");Q33=makeQuery(id+"F5.opFillet","BLEND_EDGE",EDGE,{"blendedFrom":[makeQuery(id+"F4.opExtrude","SWEPT_EDGE",EDGE,{"disambiguationData":[OSD([subQ1,subQ0])]}),makeQuery(id+"F4.opExtrude","CAP_FACE",FACE,{"disambiguationData":[OSD([sQuery(id+"F1.wireOp",EDGE,"E4"),sQuery(id+"F1.wireOp",EDGE,"E5"),subQ1,sQuery(id+"F1.wireOp",EDGE,"E7"),sQuery(id+"F1.wireOp",EDGE,"E8"),sQuery(id+"F1.wireOp",EDGE,"E9"),sQuery(id+"F1.wireOp",EDGE,"E10"),sQuery(id+"F1.wireOp",EDGE,"E11"),subQ0,sQuery(id+"F1.wireOp",EDGE,"E13.trimOffspring"),sQuery(id+"F1.wireOp",EDGE,"E14.trimOffspring"),sQuery(id+"F1.wireOp",EDGE,"E15"),sQuery(id+"F1.wireOp",EDGE,"E16.trimOffspring")])],"isStart":false})],"blendedInto":[makeQuery(id+"F4.opExtrude","CAP_FACE",FACE,{"disambiguationData":[OSD([sQuery(id+"F1.wireOp",EDGE,"E4"),sQuery(id+"F1.wireOp",EDGE,"E5"),subQ1,sQuery(id+"F1.wireOp",EDGE,"E7"),sQuery(id+"F1.wireOp",EDGE,"E8"),sQuery(id+"F1.wireOp",EDGE,"E9"),sQuery(id+"F1.wireOp",EDGE,"E10"),sQuery(id+"F1.wireOp",EDGE,"E11"),subQ0,sQuery(id+"F1.wireOp",EDGE,"E13.trimOffspring"),sQuery(id+"F1.wireOp",EDGE,"E14.trimOffspring"),sQuery(id+"F1.wireOp",EDGE,"E15"),sQuery(id+"F1.wireOp",EDGE,"E16.trimOffspring")])],"isStart":false})]});}
            var Q34;
            Q34=makeQuery(id+"F4.opExtrude","CAP_EDGE",EDGE,{"disambiguationData":[OSD([sQuery(id+"F1.wireOp",EDGE,"E6")])],"isStart":false});
            var Q35;
            {var subQ0=sQuery(id+"F1.wireOp",EDGE,"E14.trimOffspring");var subQ1=sQuery(id+"F1.wireOp",EDGE,"E11");Q35=makeQuery(id+"F5.opFillet","BLEND_EDGE",EDGE,{"blendedFrom":[makeQuery(id+"F4.opExtrude","SWEPT_EDGE",EDGE,{"disambiguationData":[OSD([subQ1,subQ0])]}),makeQuery(id+"F4.opExtrude","CAP_FACE",FACE,{"disambiguationData":[OSD([sQuery(id+"F1.wireOp",EDGE,"E4"),sQuery(id+"F1.wireOp",EDGE,"E5"),sQuery(id+"F1.wireOp",EDGE,"E6"),sQuery(id+"F1.wireOp",EDGE,"E7"),sQuery(id+"F1.wireOp",EDGE,"E8"),sQuery(id+"F1.wireOp",EDGE,"E9"),sQuery(id+"F1.wireOp",EDGE,"E10"),subQ1,sQuery(id+"F1.wireOp",EDGE,"E12.trimOffspring"),sQuery(id+"F1.wireOp",EDGE,"E13.trimOffspring"),subQ0,sQuery(id+"F1.wireOp",EDGE,"E15"),sQuery(id+"F1.wireOp",EDGE,"E16.trimOffspring")])],"isStart":false})],"blendedInto":[makeQuery(id+"F4.opExtrude","CAP_FACE",FACE,{"disambiguationData":[OSD([sQuery(id+"F1.wireOp",EDGE,"E4"),sQuery(id+"F1.wireOp",EDGE,"E5"),sQuery(id+"F1.wireOp",EDGE,"E6"),sQuery(id+"F1.wireOp",EDGE,"E7"),sQuery(id+"F1.wireOp",EDGE,"E8"),sQuery(id+"F1.wireOp",EDGE,"E9"),sQuery(id+"F1.wireOp",EDGE,"E10"),subQ1,sQuery(id+"F1.wireOp",EDGE,"E12.trimOffspring"),sQuery(id+"F1.wireOp",EDGE,"E13.trimOffspring"),subQ0,sQuery(id+"F1.wireOp",EDGE,"E15"),sQuery(id+"F1.wireOp",EDGE,"E16.trimOffspring")])],"isStart":false})]});}
            var Q36;
            Q36=makeQuery(id+"F4.opExtrude","CAP_EDGE",EDGE,{"disambiguationData":[OSD([sQuery(id+"F1.wireOp",EDGE,"E11")])],"isStart":false});
            var Q37;
            {var subQ0=sQuery(id+"F1.wireOp",EDGE,"E11");var subQ1=sQuery(id+"F1.wireOp",EDGE,"E6");Q37=makeQuery(id+"F5.opFillet","BLEND_EDGE",EDGE,{"blendedFrom":[makeQuery(id+"F4.opExtrude","SWEPT_EDGE",EDGE,{"disambiguationData":[OSD([subQ1,subQ0])]}),makeQuery(id+"F4.opExtrude","CAP_FACE",FACE,{"disambiguationData":[OSD([sQuery(id+"F1.wireOp",EDGE,"E4"),sQuery(id+"F1.wireOp",EDGE,"E5"),subQ1,sQuery(id+"F1.wireOp",EDGE,"E7"),sQuery(id+"F1.wireOp",EDGE,"E8"),sQuery(id+"F1.wireOp",EDGE,"E9"),sQuery(id+"F1.wireOp",EDGE,"E10"),subQ0,sQuery(id+"F1.wireOp",EDGE,"E12.trimOffspring"),sQuery(id+"F1.wireOp",EDGE,"E13.trimOffspring"),sQuery(id+"F1.wireOp",EDGE,"E14.trimOffspring"),sQuery(id+"F1.wireOp",EDGE,"E15"),sQuery(id+"F1.wireOp",EDGE,"E16.trimOffspring")])],"isStart":false})],"blendedInto":[makeQuery(id+"F4.opExtrude","CAP_FACE",FACE,{"disambiguationData":[OSD([sQuery(id+"F1.wireOp",EDGE,"E4"),sQuery(id+"F1.wireOp",EDGE,"E5"),subQ1,sQuery(id+"F1.wireOp",EDGE,"E7"),sQuery(id+"F1.wireOp",EDGE,"E8"),sQuery(id+"F1.wireOp",EDGE,"E9"),sQuery(id+"F1.wireOp",EDGE,"E10"),subQ0,sQuery(id+"F1.wireOp",EDGE,"E12.trimOffspring"),sQuery(id+"F1.wireOp",EDGE,"E13.trimOffspring"),sQuery(id+"F1.wireOp",EDGE,"E14.trimOffspring"),sQuery(id+"F1.wireOp",EDGE,"E15"),sQuery(id+"F1.wireOp",EDGE,"E16.trimOffspring")])],"isStart":false})]});}
            fillet(context, id + "F6", {"entities" : qUnion([Q0, Q1, Q2, Q3, Q4, Q5, Q6, Q7, Q8, Q9, Q10, Q11, Q12, Q13, Q14, Q15, Q16, Q17, Q18, Q19, Q20, Q21, Q22, Q23, Q24, Q25, Q26, Q27, Q28, Q29, Q30, Q31, Q32, Q33, Q34, Q35, Q36, Q37]), "radius" : 0.25 * mm, "tangentPropagation" : true, "allowEdgeOverflow" : false});
        }
        {
            var Q0;
            Q0=makeQuery(id+"F2.opExtrude","CAP_FACE",FACE,{"disambiguationData":[OSD([sQuery(id+"F0.wireOp",EDGE,"E0"),sQuery(id+"F0.wireOp",EDGE,"E1"),sQuery(id+"F0.wireOp",EDGE,"E2"),sQuery(id+"F0.wireOp",EDGE,"E3")])],"isStart":false});
            fillet(context, id + "F7", {"entities" : qUnion([Q0]), "radius" : 2.54 * mm, "tangentPropagation" : true, "allowEdgeOverflow" : false});
        }
        {
            var Q0;
            Q0=makeQuery(id+"F2.opExtrude","CAP_FACE",FACE,{"disambiguationData":[OSD([sQuery(id+"F0.wireOp",EDGE,"E0"),sQuery(id+"F0.wireOp",EDGE,"E1"),sQuery(id+"F0.wireOp",EDGE,"E2"),sQuery(id+"F0.wireOp",EDGE,"E3")])],"isStart":false});
            var sketch = newSketch(context, id + "F8", { "sketchPlane" : qUnion([Q0])});
            skText(sketch, "E34", { "text": "PUSH", "fontName": "OpenSans-Bold.ttf"});
            const initialGuessF8  = {"E34": [-0.00952, -0.00256, 1, 0, 0.00513]};
            skSetInitialGuess(sketch, initialGuessF8);
            skSolve(sketch);
        }
        {
            var Q0;
            Q0 = qSketchRegion(id + "F8", true);
            extrude(context, id + "F9", {"entities" : qUnion([Q0]), "operationType" : NewBodyOperationType.REMOVE, "oppositeDirection" : true, "depth" : 1.27 * mm});
        }
    });
